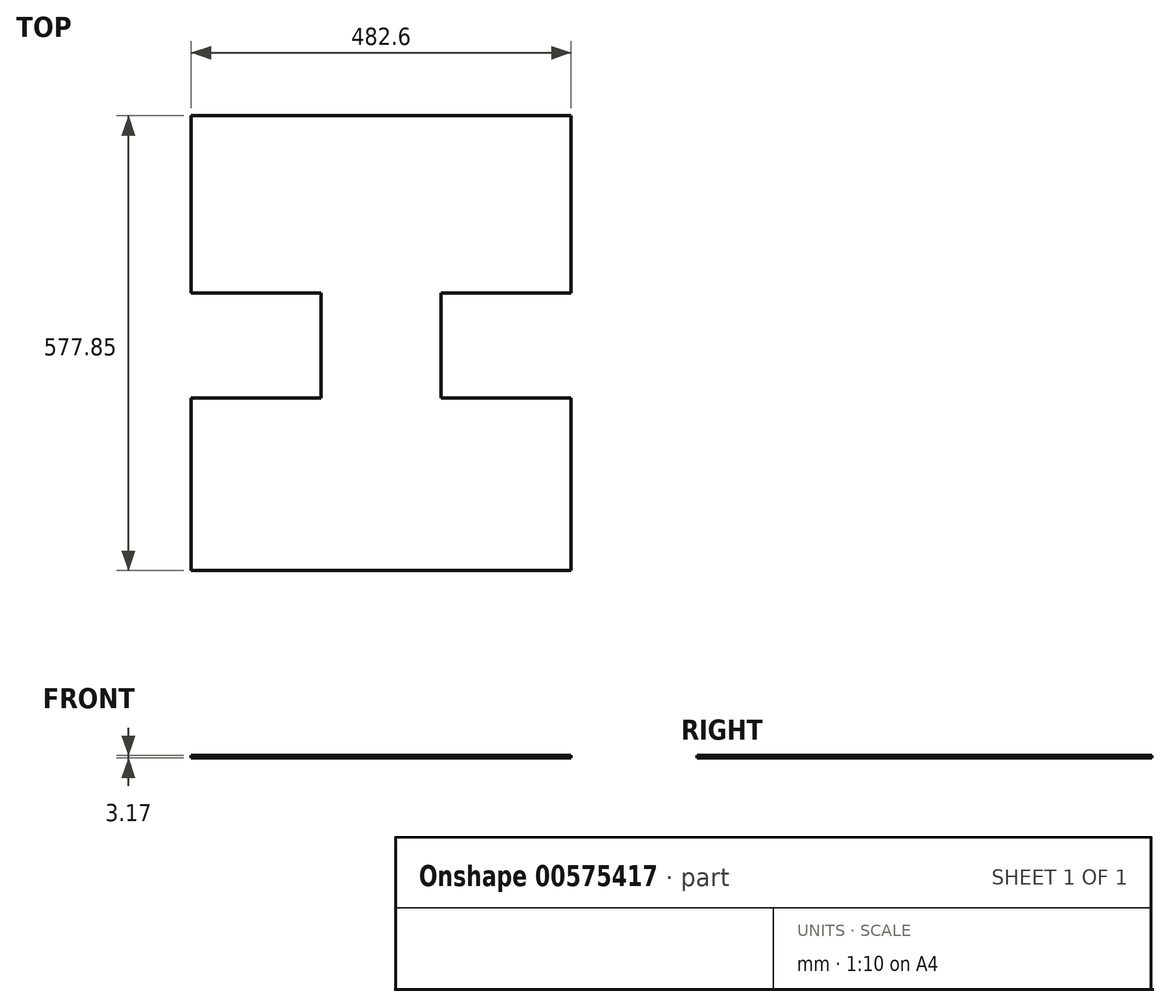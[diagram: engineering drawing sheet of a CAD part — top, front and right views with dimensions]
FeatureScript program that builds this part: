
annotation { "Feature Type Name" : "Feature", "Feature Type Description" : "" }
export const myFeature = defineFeature(function(context is Context, id is Id, definition is map)
    precondition{}
    {
        {
            var Q0;
            Q0=qCreatedBy(makeId("Top.planeOp"),FACE);
            var sketch = newSketch(context, id + "F0", { "sketchPlane" : qUnion([Q0])});
            skLineSegment(sketch, "E0.bottom", {"start": v(76.2, 66.68) * mm, "end": v(-76.2, 66.68) * mm});
            skLineSegment(sketch, "E0.top", {"start": v(76.2, -66.68) * mm, "end": v(-76.2, -66.68) * mm});
            skLineSegment(sketch, "E0.left", {"start": v(76.2, 66.68) * mm, "end": v(76.2, -66.67) * mm});
            skLineSegment(sketch, "E0.right", {"start": v(-76.2, 66.68) * mm, "end": v(-76.2, -66.67) * mm});
            skPoint(sketch, "E0.middle", {"position": v(0, 0) * mm});
            skSolve(sketch);
        }
        {
            var Q0;
            Q0=makeQuery(id+"F0.imprint","IMPRINT",FACE,{"disambiguationData":[TD([[makeQuery(id+"F0.imprint","IMPRINT",EDGE,{"derivedFrom":sQuery(id+"F0.wireOp",EDGE,"E0.bottom")}),1.0]])]});
            extrude(context, id + "F1", {"entities" : qUnion([Q0]), "depth" : 3.17 * mm, "offsetDistance" : 25.4 * mm});
        }
        {
            var Q0;
            Q0=makeQuery(id+"F1.opExtrude","CAP_FACE",FACE,{"disambiguationData":[OSD([sQuery(id+"F0.wireOp",EDGE,"E0.bottom"),sQuery(id+"F0.wireOp",EDGE,"E0.top"),sQuery(id+"F0.wireOp",EDGE,"E0.left"),sQuery(id+"F0.wireOp",EDGE,"E0.right")])],"isStart":false});
            var sketch = newSketch(context, id + "F2", { "sketchPlane" : qUnion([Q0])});
            skLineSegment(sketch, "E1.bottom", {"start": v(-241.3, 66.68) * mm, "end": v(241.3, 66.68) * mm});
            skLineSegment(sketch, "E1.top", {"start": v(-241.3, 292.1) * mm, "end": v(241.3, 292.1) * mm});
            skLineSegment(sketch, "E1.left", {"start": v(-241.3, 66.68) * mm, "end": v(-241.3, 292.1) * mm});
            skLineSegment(sketch, "E1.right", {"start": v(241.3, 66.68) * mm, "end": v(241.3, 292.1) * mm});
            skPoint(sketch, "E2.firstSnap0", {"position": v(0, -66.68) * mm});
            skLineSegment(sketch, "E2.bottom", {"start": v(241.3, -66.68) * mm, "end": v(-241.3, -66.68) * mm});
            skLineSegment(sketch, "E2.top", {"start": v(241.3, -285.75) * mm, "end": v(-241.3, -285.75) * mm});
            skLineSegment(sketch, "E2.left", {"start": v(241.3, -66.68) * mm, "end": v(241.3, -285.75) * mm});
            skLineSegment(sketch, "E2.right", {"start": v(-241.3, -66.68) * mm, "end": v(-241.3, -285.75) * mm});
            skSolve(sketch);
        }
        {
            var Q0;
            Q0=makeQuery(id+"F2.imprint","IMPRINT",FACE,{"disambiguationData":[TD([[makeQuery(id+"F2.imprint","IMPRINT",EDGE,{"derivedFrom":sQuery(id+"F2.wireOp",EDGE,"E1.top")}),-1.0]])]});
            var Q1;
            Q1=makeQuery(id+"F2.imprint","IMPRINT",FACE,{"disambiguationData":[TD([[makeQuery(id+"F2.imprint","IMPRINT",EDGE,{"derivedFrom":sQuery(id+"F2.wireOp",EDGE,"E2.top")}),-1.0]])]});
            extrude(context, id + "F3", {"entities" : qUnion([Q0, Q1]), "operationType" : NewBodyOperationType.ADD, "oppositeDirection" : true, "depth" : 3.17 * mm, "offsetDistance" : 25.4 * mm});
        }
        {
            var Q0;
            Q0=makeQuery(id+"F1.opExtrude","SWEPT_BODY",BODY,{"disambiguationData":[OSD([sQuery(id+"F0.wireOp",EDGE,"E0.bottom"),sQuery(id+"F0.wireOp",EDGE,"E0.top"),sQuery(id+"F0.wireOp",EDGE,"E0.left"),sQuery(id+"F0.wireOp",EDGE,"E0.right")])]});
            transform(context, id + "F4", {"entities" : qUnion([Q0]), "transformType" : TransformType.TRANSLATION_3D, "dx" : 0 * mm, "dy" : 0 * mm, "dz" : 0 * mm, "makeCopy" : true});
        }
        {
            var Q0;
            Q0=makeQuery(id+"F4.opPattern","COPY",BODY,{"derivedFrom":makeQuery(id+"F1.opExtrude","SWEPT_BODY",BODY,{"disambiguationData":[OSD([sQuery(id+"F0.wireOp",EDGE,"E0.bottom"),sQuery(id+"F0.wireOp",EDGE,"E0.top"),sQuery(id+"F0.wireOp",EDGE,"E0.left"),sQuery(id+"F0.wireOp",EDGE,"E0.right")])]}),"instanceName":"1"});
            deleteBodies(context, id + "F5", {"entities" : qUnion([Q0])});
        }
    });
